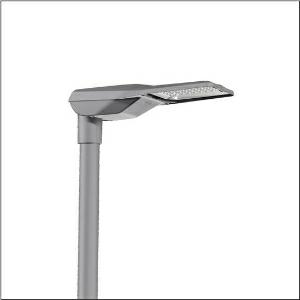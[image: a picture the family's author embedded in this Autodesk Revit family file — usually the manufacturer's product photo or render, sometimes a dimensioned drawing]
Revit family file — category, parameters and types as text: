
# Revit family: streetlight_sl_21_iq_mini___p1_0a_5xe2a31g08gb_9f18
name_source: partatom
category: Lighting Fixtures
units: mm (PartAtom-declared; Revit-internal decimal feet)

## family parameters
Cut with Voids When Loaded = No
Host = Face
Light Source = No
Part Type = Normal
Room Calculation Point = No
Round Connector Dimension = Use Diameter
Shared = No

## types (1)
- --- (1 x LED, 5680 lm, 37.1 W, 3000K)
    Apparent Load = 37 VA
    CIE Flux Codes = 21 50 90 100 100
    Color Rendering = 70
    Color Temperature = 3000K
    Default Elevation = 1800 mm
    Description = Streetlight SL 21 iQ mini, mast luminaire, primary light control with lens, of PMMA, primary optical cover: cover, of toughened safety glass, transparent, light distribution: P1.0a, light emission: direct distribution, primary light characteristic: asymmetric, installation type: post-top, side-entry, LED, High Power LED, rated luminous flux: 5.680lm, luminous efficacy: 153lm/W, light colour: 730, colour temperature: 3000K, control gear: iQ Street-Remote, control: Street-Remote, Auto-Match, Temp-Guard, Lumen-Switch, Night-Set, Smart-Wire, Light-Fading, Desk-Remote (wireless, voltage-free reading and setting of iQ features in the workshop via application-optimized NFC function/RFID function), optimised constant luminous flux control (CLO 2.0), pre-setting: linear dimming characteristic, mains connection: 220..240V, AC, 50/60Hz, start of lifetime: 37W, end of service life: 39W, reduction: 18W, luminaire housing, of diecast aluminium, powder-coated, SITECO metallic grey (DB 702S), corrosivity category C5 high according to DIN EN ISO 12944, please order mast flange separately, inclination adjustable: 0°, 5°, 10°, 15°, sealing non-destructively replaceable, multi-level sealing system, length: 628mm, width: 235mm, height: 110mm, mast flange for spigot size: 42mm (side-entry): 5XC10008XM4, 60/48mm (side-entry/post-top): 5XC10108XM2, 76/60mm (side-entry/post-top): 5XC10108XM1, mounting height: 4..8m, protection rating (complete): IP66, insulation class (complete): insulation class II (safety insulation), certification: CE, ENEC, ENEC+, VDE, impact resistance: IK10, permissible operating ambient temperature for outdoor applications: -40..+50°C, standard-compliant lighting for roads and squares, packaging unit: 1 piece

Light Distribution: P1.0a
    Height = 110 mm
    Lamp = 1 x LED
    Lamp Light Flux = 5680 lm
    Lamp Power = 37.1 W
    Lamp count = 1
    Length = 625 mm
    Luminous efficacy = 153 lm/W
    Manufacturer = Siteco
    ModVariant = No
    Model = 5XE2A31G08GB
    Number of Poles = 1
    OnlyDefault = Yes
    Power Factor = 1
    Product Name = Streetlight SL 21 iQ mini | P1.0a
    Product group = mast luminaire | pylon top
    ProductGroupID = 6100
    Protection Class = Protection class II
    Protection Degree = IP 66
    RLX_Detail_Level = 1
    RLX_Emergency_Light_Flux = 0 lm
    RLX_Emergency_Type = 0
    RLX_Emergency_Type_DB = No
    RlxData = <blob elided: 37589 chars, md5=183e8a63>
    Socket = socket
    Standby Power = 0 W
    System Light Flux = 5680 lm
    System Power = 37 W
    Type Comments = factory setting: luminous flux: 100 % | dim-lin: 254 | 385 mA
    Type Image = l_1003519.jpg
    URL = http://relux.com
    VarID = @adj_184279
    Voltage = 0 V
    Weight = 0.00 kg
    Width = 234 mm

## geometry (parser evidence)
native form markers: Blend x4, Sweep x9
no freeform markers — native parametric forms only
